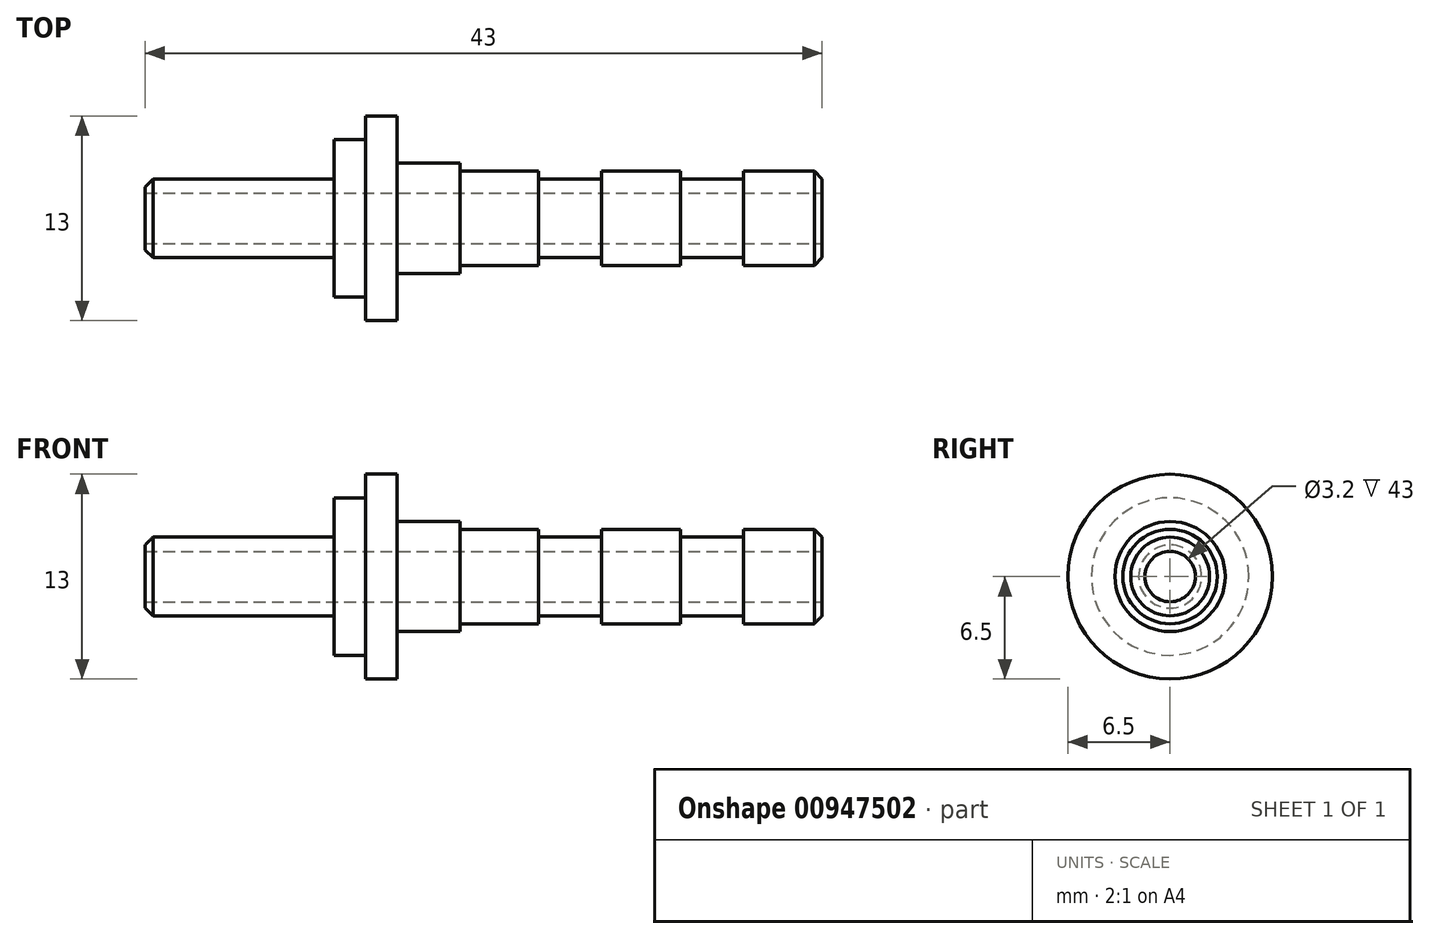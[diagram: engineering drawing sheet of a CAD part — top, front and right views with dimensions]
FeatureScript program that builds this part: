
annotation { "Feature Type Name" : "Feature", "Feature Type Description" : "" }
export const myFeature = defineFeature(function(context is Context, id is Id, definition is map)
    precondition{}
    {
        {
            var Q0;
            Q0=qCreatedBy(makeId("Front.planeOp"),FACE);
            var sketch = newSketch(context, id + "F0", { "sketchPlane" : qUnion([Q0])});
            skLineSegment(sketch, "E0", {"start": v(0, 0) * mm, "end": v(43, 0) * mm});
            skLineSegment(sketch, "E1", {"start": v(43, 0) * mm, "end": v(43, 3) * mm});
            skLineSegment(sketch, "E2", {"start": v(43, 3) * mm, "end": v(38, 3) * mm});
            skLineSegment(sketch, "E3", {"start": v(38, 3) * mm, "end": v(38, 2.5) * mm});
            skLineSegment(sketch, "E4", {"start": v(38, 2.5) * mm, "end": v(34, 2.5) * mm});
            skLineSegment(sketch, "E5", {"start": v(34, 2.5) * mm, "end": v(34, 3) * mm});
            skLineSegment(sketch, "E6", {"start": v(34, 3) * mm, "end": v(29, 3) * mm});
            skLineSegment(sketch, "E7", {"start": v(29, 3) * mm, "end": v(29, 2.5) * mm});
            skLineSegment(sketch, "E8", {"start": v(29, 2.5) * mm, "end": v(25, 2.5) * mm});
            skLineSegment(sketch, "E9", {"start": v(25, 2.5) * mm, "end": v(25, 3) * mm});
            skLineSegment(sketch, "E10", {"start": v(25, 3) * mm, "end": v(20, 3) * mm});
            skLineSegment(sketch, "E11", {"start": v(20, 3) * mm, "end": v(20, 3.5) * mm});
            skLineSegment(sketch, "E12", {"start": v(20, 3.5) * mm, "end": v(16, 3.5) * mm});
            skLineSegment(sketch, "E13", {"start": v(16, 3.5) * mm, "end": v(16, 6.5) * mm});
            skLineSegment(sketch, "E14", {"start": v(16, 6.5) * mm, "end": v(14, 6.5) * mm});
            skLineSegment(sketch, "E15", {"start": v(14, 6.5) * mm, "end": v(14, 5) * mm});
            skLineSegment(sketch, "E16", {"start": v(14, 5) * mm, "end": v(12, 5) * mm});
            skLineSegment(sketch, "E17", {"start": v(12, 5) * mm, "end": v(12, 2.5) * mm});
            skLineSegment(sketch, "E18", {"start": v(12, 2.5) * mm, "end": v(0, 2.5) * mm});
            skLineSegment(sketch, "E19", {"start": v(0, 2.5) * mm, "end": v(0, 0) * mm});
            skLineSegment(sketch, "E20", {"start": v(0, 0) * mm, "end": v(-5.42, 0) * mm, "construction": true});
            skSolve(sketch);
        }
        {
            var Q0;
            Q0 = qSketchRegion(id + "F0", true);
            var Q1;
            Q1=sQuery(id+"F0.wireOp",EDGE,"E20");
            revolve(context, id + "F1", {"surfaceOperationType" : NewSurfaceOperationType.NEW, "entities" : qUnion([Q0]), "axis" : qUnion([Q1]), "revolveType" : RevolveType.FULL});
        }
        {
            var Q0;
            Q0=makeQuery(id+"F1.opRevolve","SWEPT_FACE",FACE,{"disambiguationData":[OSD([sQuery(id+"F0.wireOp",EDGE,"E1")])]});
            var sketch = newSketch(context, id + "F2", { "sketchPlane" : qUnion([Q0])});
            skCircle(sketch, "E21", {"center": v(0, 0) * mm, "radius": 1.6 * mm});
            skSolve(sketch);
        }
        {
            var Q0;
            Q0 = qSketchRegion(id + "F2", true);
            extrude(context, id + "F3", {"entities" : qUnion([Q0]), "operationType" : NewBodyOperationType.REMOVE, "endBound" : BoundingType.THROUGH_ALL, "oppositeDirection" : true, "depth" : 25 * mm, "offsetDistance" : 25 * mm});
        }
        {
            var Q0;
            Q0=makeQuery(id+"F1.opRevolve","SWEPT_EDGE",EDGE,{"disambiguationData":[OSD([sQuery(id+"F0.wireOp",EDGE,"E1"),sQuery(id+"F0.wireOp",EDGE,"E2")])]});
            var Q1;
            Q1=makeQuery(id+"F1.opRevolve","SWEPT_EDGE",EDGE,{"disambiguationData":[OSD([sQuery(id+"F0.wireOp",EDGE,"E18"),sQuery(id+"F0.wireOp",EDGE,"E19")])]});
            chamfer(context, id + "F4", {"entities" : qUnion([Q0, Q1]), "width" : 0.5 * mm, "tangentPropagation" : true});
        }
    });
